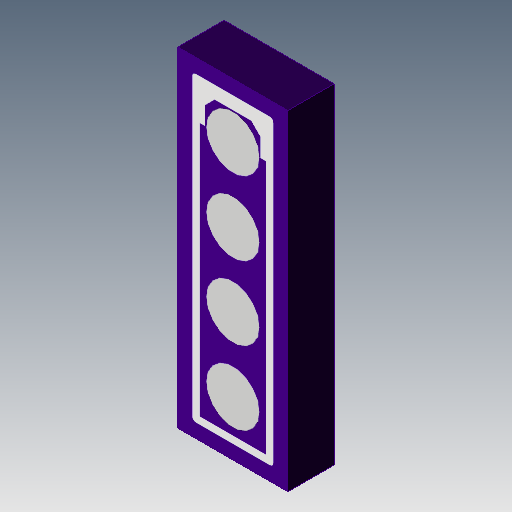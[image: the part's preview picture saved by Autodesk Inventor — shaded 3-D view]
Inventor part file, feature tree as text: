
AUTODESK INVENTOR PART (.ipt)
format: ipt  version: 2018 (Build 220112000, 112)  size: 130,560 bytes
history: native  units: mm
features: other x4, sketch x2
ambient origin geometry x8: Origin, YZ Plane, XZ Plane, XY Plane, X Axis, Y Axis, Z Axis, Center Point
bodies: Solid1 (feature_tree)
feature tree (6):
  other  "Decal1"
  other  "Decal2"
  sketch  "Sketch1"
  other  "Image1"
  sketch  "Sketch2"
  other  "Image2"
